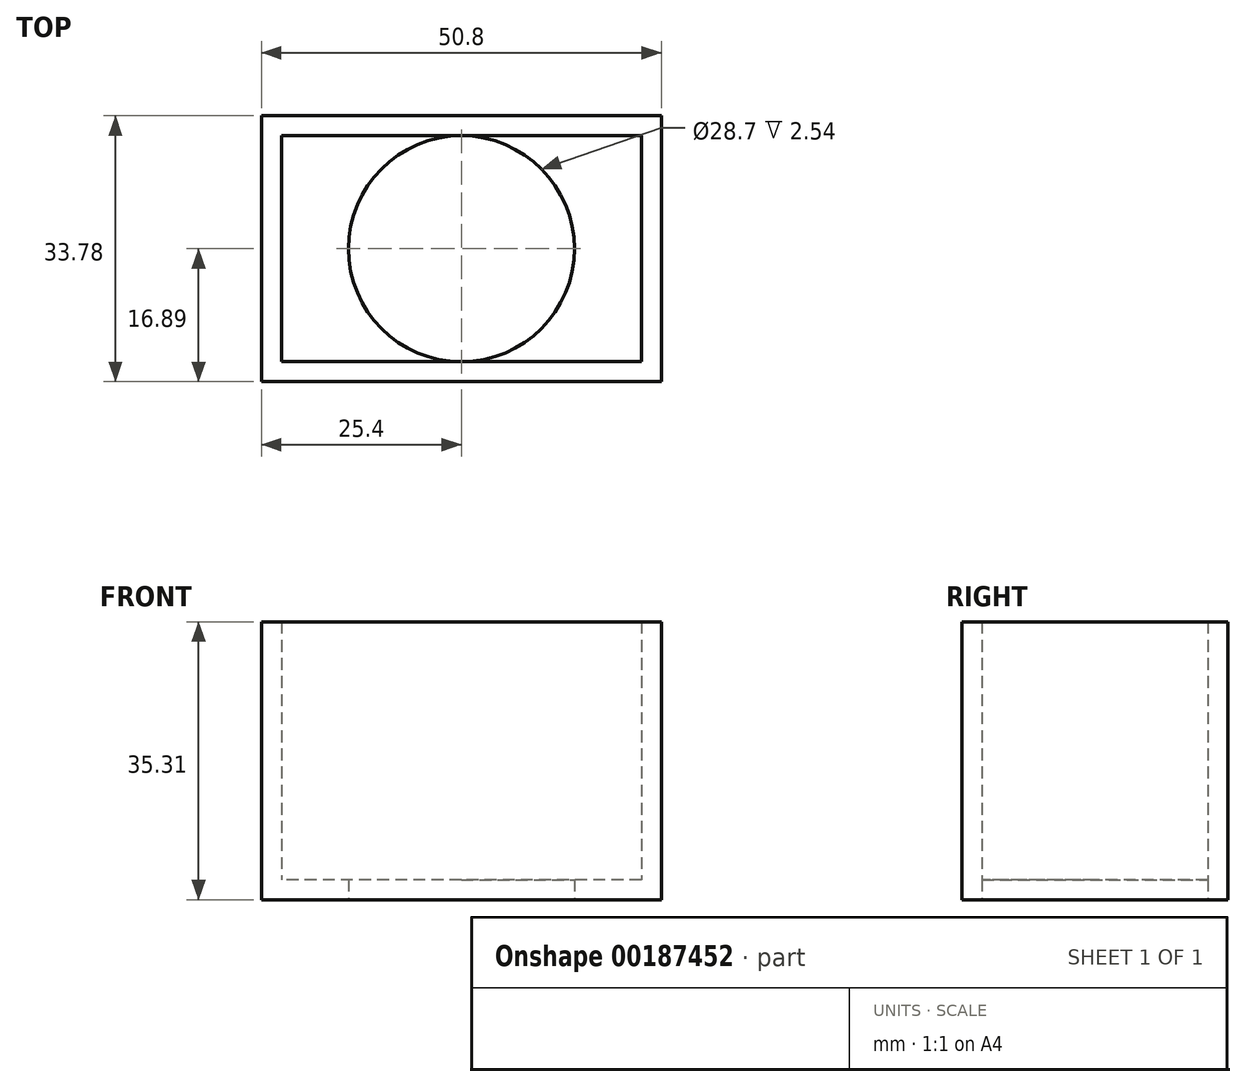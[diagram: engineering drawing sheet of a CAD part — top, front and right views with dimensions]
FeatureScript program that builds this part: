
annotation { "Feature Type Name" : "Feature", "Feature Type Description" : "" }
export const myFeature = defineFeature(function(context is Context, id is Id, definition is map)
    precondition{}
    {
        {
            var Q0;
            Q0=qCreatedBy(makeId("Top.planeOp"),FACE);
            var sketch = newSketch(context, id + "F0", { "sketchPlane" : qUnion([Q0])});
            skLineSegment(sketch, "E0.bottom", {"start": v(25.4, 16.9) * mm, "end": v(-25.4, 16.9) * mm});
            skLineSegment(sketch, "E0.top", {"start": v(25.4, -16.9) * mm, "end": v(-25.4, -16.9) * mm});
            skLineSegment(sketch, "E0.left", {"start": v(25.4, 16.9) * mm, "end": v(25.4, -16.9) * mm});
            skLineSegment(sketch, "E0.right", {"start": v(-25.4, 16.9) * mm, "end": v(-25.4, -16.9) * mm});
            skPoint(sketch, "E0.middle", {"position": v(0, 0) * mm});
            skSolve(sketch);
        }
        {
            var Q0;
            Q0=makeQuery(id+"F0.imprint","IMPRINT",FACE,{"disambiguationData":[TD([[makeQuery(id+"F0.imprint","IMPRINT",EDGE,{"derivedFrom":sQuery(id+"F0.wireOp",EDGE,"E0.bottom")}),1.0]])]});
            extrude(context, id + "F1", {"entities" : qUnion([Q0]), "depth" : 35.3 * mm});
        }
        {
            var Q0;
            Q0=makeQuery(id+"F1.opExtrude","CAP_FACE",FACE,{"disambiguationData":[OSD([sQuery(id+"F0.wireOp",EDGE,"E0.bottom"),sQuery(id+"F0.wireOp",EDGE,"E0.top"),sQuery(id+"F0.wireOp",EDGE,"E0.left"),sQuery(id+"F0.wireOp",EDGE,"E0.right")])],"isStart":false});
            shell(context, id + "F2", {"entities" : qUnion([Q0]), "thickness" : 2.54 * mm});
        }
        {
            var Q0;
            Q0=makeQuery(id+"F1.opExtrude","CAP_FACE",FACE,{"disambiguationData":[OSD([sQuery(id+"F0.wireOp",EDGE,"E0.bottom"),sQuery(id+"F0.wireOp",EDGE,"E0.top"),sQuery(id+"F0.wireOp",EDGE,"E0.left"),sQuery(id+"F0.wireOp",EDGE,"E0.right")])],"isStart":true});
            var sketch = newSketch(context, id + "F3", { "sketchPlane" : qUnion([Q0])});
            skCircle(sketch, "E1", {"center": v(0, 0) * mm, "radius": 14.35 * mm});
            skSolve(sketch);
        }
        {
            var Q0;
            Q0=makeQuery(id+"F3.imprint","IMPRINT",FACE,{"disambiguationData":[TD([[makeQuery(id+"F3.imprint","IMPRINT",EDGE,{"derivedFrom":sQuery(id+"F3.wireOp",EDGE,"E1")}),1.0]])]});
            extrude(context, id + "F4", {"entities" : qUnion([Q0]), "operationType" : NewBodyOperationType.REMOVE, "oppositeDirection" : true, "depth" : 25.4 * mm});
        }
    });
